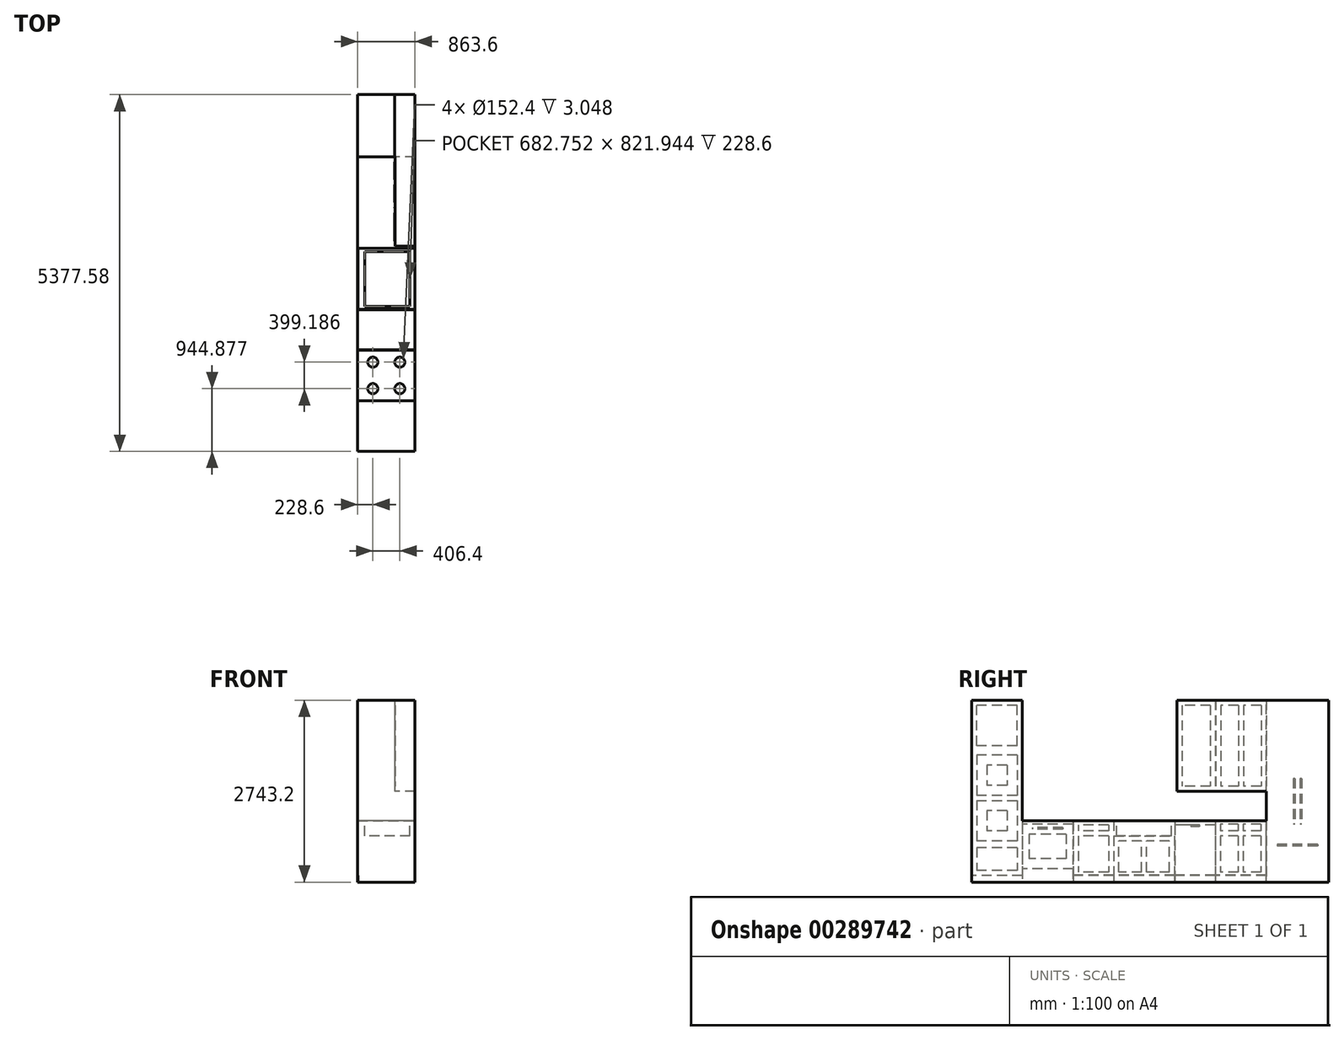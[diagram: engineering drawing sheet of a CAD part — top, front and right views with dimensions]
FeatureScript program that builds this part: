
annotation { "Feature Type Name" : "Feature", "Feature Type Description" : "" }
export const myFeature = defineFeature(function(context is Context, id is Id, definition is map)
    precondition{}
    {
        {
            var Q0;
            Q0=qCreatedBy(makeId("Top.planeOp"),FACE);
            var sketch = newSketch(context, id + "F0", { "sketchPlane" : qUnion([Q0])});
            skLineSegment(sketch, "E0.bottom", {"start": v(431.8, -2688.8) * mm, "end": v(-431.8, -2688.8) * mm});
            skLineSegment(sketch, "E0.top", {"start": v(431.8, 2688.8) * mm, "end": v(-431.8, 2688.8) * mm});
            skLineSegment(sketch, "E0.left", {"start": v(431.8, -2688.8) * mm, "end": v(431.8, 2688.8) * mm});
            skLineSegment(sketch, "E0.right", {"start": v(-431.8, -2688.8) * mm, "end": v(-431.8, 2688.8) * mm});
            skPoint(sketch, "E0.middle", {"position": v(0, 0) * mm});
            skLineSegment(sketch, "E1.bottom", {"start": v(431.8, 1774.4) * mm, "end": v(127, 1774.4) * mm});
            skLineSegment(sketch, "E1.top", {"start": v(431.8, 402.8) * mm, "end": v(127, 402.8) * mm});
            skLineSegment(sketch, "E1.left", {"start": v(431.8, 1774.4) * mm, "end": v(431.8, 402.8) * mm});
            skLineSegment(sketch, "E1.right", {"start": v(127, 1774.4) * mm, "end": v(127, 402.8) * mm});
            skLineSegment(sketch, "E2.top", {"start": v(431.8, 2688.8) * mm, "end": v(127, 2688.8) * mm});
            skLineSegment(sketch, "E2.left", {"start": v(431.8, 1774.4) * mm, "end": v(431.8, 2688.8) * mm});
            skLineSegment(sketch, "E2.right", {"start": v(127, 1774.4) * mm, "end": v(127, 2688.8) * mm});
            skSolve(sketch);
        }
        {
            var Q0;
            {var subQ4=sQuery(id+"F0.wireOp",EDGE,"E1.bottom");Q0=makeQuery(id+"F0.imprint","IMPRINT",FACE,{"disambiguationData":[TD([[makeQuery(id+"F0.imprint","IMPRINT",EDGE,{"derivedFrom":subQ4}),-1.0]])]});}
            var Q1;
            {var subQ0=sQuery(id+"F0.wireOp",EDGE,"E1.bottom");Q1=makeQuery(id+"F0.imprint","IMPRINT",FACE,{"disambiguationData":[TD([[makeQuery(id+"F0.imprint","IMPRINT",EDGE,{"derivedFrom":subQ0}),1.0]])]});}
            var Q2;
            {var subQ1=sQuery(id+"F0.wireOp",EDGE,"E0.bottom");Q2=makeQuery(id+"F0.imprint","IMPRINT",FACE,{"disambiguationData":[TD([[makeQuery(id+"F0.imprint","IMPRINT",EDGE,{"derivedFrom":subQ1}),-1.0]])]});}
            extrude(context, id + "F1", {"entities" : qUnion([Q0, Q1, Q2]), "depth" : 2743.2 * mm, "offsetDistance" : 30.48 * mm});
        }
        {
            var Q0;
            Q0=makeQuery(id+"F1.opExtrude","CAP_FACE",FACE,{"disambiguationData":[OSD([sQuery(id+"F0.wireOp",EDGE,"E0.bottom"),sQuery(id+"F0.wireOp",EDGE,"E0.top"),sQuery(id+"F0.wireOp",EDGE,"E0.left"),sQuery(id+"F0.wireOp",EDGE,"E0.right")])],"isStart":false});
            var sketch = newSketch(context, id + "F2", { "sketchPlane" : qUnion([Q0])});
            skLineSegment(sketch, "E3.bottom", {"start": v(431.8, 2688.8) * mm, "end": v(127, 2688.8) * mm});
            skLineSegment(sketch, "E3.top", {"start": v(431.8, 402.8) * mm, "end": v(127, 402.8) * mm});
            skLineSegment(sketch, "E3.left", {"start": v(431.8, 2688.8) * mm, "end": v(431.8, 402.8) * mm});
            skLineSegment(sketch, "E3.right", {"start": v(127, 2688.8) * mm, "end": v(127, 402.8) * mm});
            skLineSegment(sketch, "E4", {"start": v(127, 1749) * mm, "end": v(-431.8, 1749) * mm});
            skLineSegment(sketch, "E5.bottom", {"start": v(431.8, -2688.8) * mm, "end": v(-431.8, -2688.8) * mm});
            skLineSegment(sketch, "E5.top", {"start": v(431.8, -1926.8) * mm, "end": v(-431.8, -1926.8) * mm});
            skLineSegment(sketch, "E5.left", {"start": v(431.8, -2688.8) * mm, "end": v(431.8, -1926.8) * mm});
            skLineSegment(sketch, "E5.right", {"start": v(-431.8, -2688.8) * mm, "end": v(-431.8, -1926.8) * mm});
            skSolve(sketch);
        }
        {
            var Q0;
            {var subQ3=sQuery(id+"F2.wireOp",EDGE,"E3.top");Q0=makeQuery(id+"F2.imprint","IMPRINT",FACE,{"disambiguationData":[TD([[makeQuery(id+"F2.imprint","IMPRINT",EDGE,{"derivedFrom":subQ3}),1.0]])]});}
            extrude(context, id + "F3", {"entities" : qUnion([Q0]), "operationType" : NewBodyOperationType.REMOVE, "oppositeDirection" : true, "depth" : 1371.6 * mm, "offsetDistance" : 30.48 * mm});
        }
        {
            var Q0;
            {var subQ0=sQuery(id+"F0.wireOp",EDGE,"E0.right");var subQ1=sQuery(id+"F0.wireOp",EDGE,"E0.left");var subQ2=sQuery(id+"F0.wireOp",EDGE,"E0.top");Q0=makeQuery(id+"F3.boolean.opBoolean","SPLIT",FACE,{"disambiguationData":[TD([makeQuery(id+"F1.opExtrude","SWEPT_FACE",FACE,{"disambiguationData":[OSD([subQ2])]})])],"derivedFrom":makeQuery(id+"F1.opExtrude","CAP_FACE",FACE,{"disambiguationData":[OSD([sQuery(id+"F0.wireOp",EDGE,"E0.bottom"),subQ2,subQ1,subQ0])],"isStart":false})});}
            var sketch = newSketch(context, id + "F4", { "sketchPlane" : qUnion([Q0])});
            skLineSegment(sketch, "E6", {"start": v(127, 1749) * mm, "end": v(127, 2688.8) * mm});
            skSolve(sketch);
        }
        {
            var Q0;
            {var subQ0=sQuery(id+"F4.wireOp",EDGE,"E6");Q0=makeQuery(id+"F4.imprint","IMPRINT",FACE,{"disambiguationData":[TD([[makeQuery(id+"F4.imprint","IMPRINT",EDGE,{"derivedFrom":subQ0}),1.0]])]});}
            extrude(context, id + "F5", {"entities" : qUnion([Q0]), "operationType" : NewBodyOperationType.REMOVE, "oppositeDirection" : true, "depth" : (((9 * 12) - 70.5) / 12) * mm, "offsetDistance" : 30.48 * mm});
        }
        {
            var Q0;
            Q0=makeQuery(id+"F1.opExtrude","SWEPT_FACE",FACE,{"disambiguationData":[OSD([sQuery(id+"F0.wireOp",EDGE,"E0.right")])]});
            var sketch = newSketch(context, id + "F6", { "sketchPlane" : qUnion([Q0])});
            skLineSegment(sketch, "E7", {"start": v(-1749, 1371.6) * mm, "end": v(-1749, 927.1) * mm});
            skLineSegment(sketch, "E8", {"start": v(-1749, 927.1) * mm, "end": v(1926.8, 927.1) * mm});
            skLineSegment(sketch, "E9", {"start": v(1926.8, 927.1) * mm, "end": v(1926.8, 1371.6) * mm});
            skSolve(sketch);
        }
        {
            var Q0;
            Q0=makeQuery(id+"F6.imprint","IMPRINT",FACE,{"disambiguationData":[TD([[makeQuery(id+"F6.imprint","IMPRINT",EDGE,{"derivedFrom":sQuery(id+"F6.wireOp",EDGE,"E7")}),1.0]])]});
            extrude(context, id + "F7", {"entities" : qUnion([Q0]), "operationType" : NewBodyOperationType.REMOVE, "oppositeDirection" : true, "depth" : 1219.2 * mm, "offsetDistance" : 30.48 * mm});
        }
        {
            var Q0;
            Q0=makeQuery(id+"F1.opExtrude","SWEPT_FACE",FACE,{"disambiguationData":[OSD([sQuery(id+"F0.wireOp",EDGE,"E0.right")])]});
            var sketch = newSketch(context, id + "F8", { "sketchPlane" : qUnion([Q0])});
            skLineSegment(sketch, "E10.bottom", {"start": v(-2282.4, 1562.1) * mm, "end": v(-2257, 1562.1) * mm});
            skLineSegment(sketch, "E10.top", {"start": v(-2282.4, 876.3) * mm, "end": v(-2257, 876.3) * mm});
            skLineSegment(sketch, "E10.left", {"start": v(-2282.4, 1562.1) * mm, "end": v(-2282.4, 876.3) * mm});
            skLineSegment(sketch, "E10.right", {"start": v(-2257, 1562.1) * mm, "end": v(-2257, 876.3) * mm});
            skLineSegment(sketch, "E11.bottom", {"start": v(-2180.8, 1562.1) * mm, "end": v(-2155.4, 1562.1) * mm});
            skLineSegment(sketch, "E11.top", {"start": v(-2180.8, 876.3) * mm, "end": v(-2155.4, 876.3) * mm});
            skLineSegment(sketch, "E11.left", {"start": v(-2180.8, 1562.1) * mm, "end": v(-2180.8, 876.3) * mm});
            skLineSegment(sketch, "E11.right", {"start": v(-2155.4, 1562.1) * mm, "end": v(-2155.4, 876.3) * mm});
            skLineSegment(sketch, "E12", {"start": v(-2218.9, 1790.7) * mm, "end": v(-2218.9, 0) * mm, "construction": true});
            skLineSegment(sketch, "E13.bottom", {"start": v(-2523.7, 571.5) * mm, "end": v(-1914.1, 571.5) * mm});
            skLineSegment(sketch, "E13.top", {"start": v(-2523.7, 546.1) * mm, "end": v(-1914.1, 546.1) * mm});
            skLineSegment(sketch, "E13.left", {"start": v(-2523.7, 571.5) * mm, "end": v(-2523.7, 546.1) * mm});
            skLineSegment(sketch, "E13.right", {"start": v(-1914.1, 571.5) * mm, "end": v(-1914.1, 546.1) * mm});
            skLineSegment(sketch, "E14.left", {"start": v(-1749, 927.1) * mm, "end": v(-1749, 0) * mm});
            skLineSegment(sketch, "E14.right", {"start": v(-1745.95, 927.1) * mm, "end": v(-1745.95, 0) * mm});
            skLineSegment(sketch, "E15.left", {"start": v(-983.95, 927.1) * mm, "end": v(-983.95, 0) * mm});
            skLineSegment(sketch, "E15.right", {"start": v(-980.9, 927.1) * mm, "end": v(-980.9, 0) * mm});
            skLineSegment(sketch, "E16.bottom", {"start": v(-371.3, 927.1) * mm, "end": v(-368.25, 927.1) * mm});
            skLineSegment(sketch, "E16.top", {"start": v(-371.3, 0) * mm, "end": v(-368.25, 0) * mm});
            skLineSegment(sketch, "E16.left", {"start": v(-371.3, 927.1) * mm, "end": v(-371.3, 0) * mm});
            skLineSegment(sketch, "E16.right", {"start": v(-368.25, 927.1) * mm, "end": v(-368.25, 0) * mm});
            skLineSegment(sketch, "E17.bottom", {"start": v(546.15, 927.1) * mm, "end": v(549.2, 927.1) * mm});
            skLineSegment(sketch, "E17.top", {"start": v(546.15, 0) * mm, "end": v(549.2, 0) * mm});
            skLineSegment(sketch, "E17.left", {"start": v(546.15, 927.1) * mm, "end": v(546.15, 0) * mm});
            skLineSegment(sketch, "E17.right", {"start": v(549.2, 927.1) * mm, "end": v(549.2, 0) * mm});
            skLineSegment(sketch, "E18.bottom", {"start": v(1158.8, 927.1) * mm, "end": v(1161.85, 927.1) * mm});
            skLineSegment(sketch, "E18.top", {"start": v(1158.8, 0) * mm, "end": v(1161.85, 0) * mm});
            skLineSegment(sketch, "E18.left", {"start": v(1158.8, 927.1) * mm, "end": v(1158.8, 0) * mm});
            skLineSegment(sketch, "E18.right", {"start": v(1161.85, 927.1) * mm, "end": v(1161.85, 0) * mm});
            skLineSegment(sketch, "E19.bottom", {"start": v(1923.85, 927.1) * mm, "end": v(1926.9, 927.1) * mm});
            skLineSegment(sketch, "E19.top", {"start": v(1923.85, 0) * mm, "end": v(1926.9, 0) * mm});
            skLineSegment(sketch, "E19.left", {"start": v(1923.85, 927.1) * mm, "end": v(1923.85, 0) * mm});
            skLineSegment(sketch, "E19.right", {"start": v(1926.9, 927.1) * mm, "end": v(1926.9, 0) * mm});
            skLineSegment(sketch, "E20.bottom", {"start": v(-1669.75, 876.3) * mm, "end": v(-1403.05, 876.3) * mm});
            skLineSegment(sketch, "E20.top", {"start": v(-1669.75, 774.7) * mm, "end": v(-1403.05, 774.7) * mm});
            skLineSegment(sketch, "E20.left", {"start": v(-1669.75, 876.3) * mm, "end": v(-1669.75, 774.7) * mm});
            skLineSegment(sketch, "E20.right", {"start": v(-1403.05, 876.3) * mm, "end": v(-1403.05, 774.7) * mm});
            skLineSegment(sketch, "E21.bottom", {"start": v(-1326.85, 876.3) * mm, "end": v(-1060.15, 876.3) * mm});
            skLineSegment(sketch, "E21.top", {"start": v(-1326.85, 774.7) * mm, "end": v(-1060.15, 774.7) * mm});
            skLineSegment(sketch, "E21.left", {"start": v(-1326.85, 876.3) * mm, "end": v(-1326.85, 774.7) * mm});
            skLineSegment(sketch, "E21.right", {"start": v(-1060.15, 876.3) * mm, "end": v(-1060.15, 774.7) * mm});
            skLineSegment(sketch, "E22", {"start": v(-1364.95, 927.1) * mm, "end": v(-1364.95, 0) * mm, "construction": true});
            skLineSegment(sketch, "E23.bottom", {"start": v(-1669.75, 698.5) * mm, "end": v(-1403.05, 698.5) * mm});
            skLineSegment(sketch, "E23.top", {"start": v(-1669.75, 152.4) * mm, "end": v(-1403.05, 152.4) * mm});
            skLineSegment(sketch, "E23.left", {"start": v(-1669.75, 698.5) * mm, "end": v(-1669.75, 152.4) * mm});
            skLineSegment(sketch, "E23.right", {"start": v(-1403.05, 698.5) * mm, "end": v(-1403.05, 152.4) * mm});
            skLineSegment(sketch, "E24.bottom", {"start": v(-1326.85, 698.5) * mm, "end": v(-1060.15, 698.5) * mm});
            skLineSegment(sketch, "E24.top", {"start": v(-1326.85, 152.4) * mm, "end": v(-1060.15, 152.4) * mm});
            skLineSegment(sketch, "E24.left", {"start": v(-1326.85, 698.5) * mm, "end": v(-1326.85, 152.4) * mm});
            skLineSegment(sketch, "E24.right", {"start": v(-1060.15, 698.5) * mm, "end": v(-1060.15, 152.4) * mm});
            skLineSegment(sketch, "E25.bottom", {"start": v(-980.9, 863.6) * mm, "end": v(-371.3, 863.6) * mm});
            skLineSegment(sketch, "E25.top", {"start": v(-980.9, 860.55) * mm, "end": v(-371.3, 860.55) * mm});
            skLineSegment(sketch, "E25.left", {"start": v(-980.9, 863.6) * mm, "end": v(-980.9, 860.55) * mm});
            skLineSegment(sketch, "E25.right", {"start": v(-371.3, 863.6) * mm, "end": v(-371.3, 860.55) * mm});
            skLineSegment(sketch, "E26.bottom", {"start": v(-739.6, 860.55) * mm, "end": v(-612.6, 860.55) * mm});
            skLineSegment(sketch, "E26.top", {"start": v(-739.6, 835.15) * mm, "end": v(-612.6, 835.15) * mm});
            skLineSegment(sketch, "E26.left", {"start": v(-739.6, 860.55) * mm, "end": v(-739.6, 835.15) * mm});
            skLineSegment(sketch, "E26.right", {"start": v(-612.6, 860.55) * mm, "end": v(-612.6, 835.15) * mm});
            skLineSegment(sketch, "E27", {"start": v(-676.1, 927.1) * mm, "end": v(-676.1, 0) * mm, "construction": true});
            skLineSegment(sketch, "E28.bottom", {"start": v(-980.9, 104.65) * mm, "end": v(-371.3, 104.65) * mm});
            skLineSegment(sketch, "E28.top", {"start": v(-980.9, 101.6) * mm, "end": v(-371.3, 101.6) * mm});
            skLineSegment(sketch, "E28.left", {"start": v(-980.9, 104.65) * mm, "end": v(-980.9, 101.6) * mm});
            skLineSegment(sketch, "E28.right", {"start": v(-371.3, 104.65) * mm, "end": v(-371.3, 101.6) * mm});
            skLineSegment(sketch, "E29.bottom", {"start": v(546.15, 698.5) * mm, "end": v(-368.25, 698.5) * mm});
            skLineSegment(sketch, "E29.top", {"start": v(546.15, 695.45) * mm, "end": v(-368.25, 695.45) * mm});
            skLineSegment(sketch, "E29.left", {"start": v(546.15, 698.5) * mm, "end": v(546.15, 695.45) * mm});
            skLineSegment(sketch, "E29.right", {"start": v(-368.25, 698.5) * mm, "end": v(-368.25, 695.45) * mm});
            skLineSegment(sketch, "E30.bottom", {"start": v(-292.05, 152.4) * mm, "end": v(50.85, 152.4) * mm});
            skLineSegment(sketch, "E30.top", {"start": v(-292.05, 619.25) * mm, "end": v(50.85, 619.25) * mm});
            skLineSegment(sketch, "E30.left", {"start": v(-292.05, 152.4) * mm, "end": v(-292.05, 619.25) * mm});
            skLineSegment(sketch, "E30.right", {"start": v(50.85, 152.4) * mm, "end": v(50.85, 619.25) * mm});
            skLineSegment(sketch, "E31.bottom", {"start": v(127.05, 152.4) * mm, "end": v(469.95, 152.4) * mm});
            skLineSegment(sketch, "E31.top", {"start": v(127.05, 619.25) * mm, "end": v(469.95, 619.25) * mm});
            skLineSegment(sketch, "E31.left", {"start": v(127.05, 152.4) * mm, "end": v(127.05, 619.25) * mm});
            skLineSegment(sketch, "E31.right", {"start": v(469.95, 152.4) * mm, "end": v(469.95, 619.25) * mm});
            skLineSegment(sketch, "E32", {"start": v(88.95, 695.45) * mm, "end": v(88.95, 0) * mm, "construction": true});
            skLineSegment(sketch, "E33.bottom", {"start": v(-1745.95, 104.65) * mm, "end": v(-983.95, 104.65) * mm});
            skLineSegment(sketch, "E33.top", {"start": v(-1745.95, 101.6) * mm, "end": v(-983.95, 101.6) * mm});
            skLineSegment(sketch, "E33.left", {"start": v(-1745.95, 104.65) * mm, "end": v(-1745.95, 101.6) * mm});
            skLineSegment(sketch, "E33.right", {"start": v(-983.95, 104.65) * mm, "end": v(-983.95, 101.6) * mm});
            skLineSegment(sketch, "E34.bottom", {"start": v(-368.25, 104.65) * mm, "end": v(546.15, 104.65) * mm});
            skLineSegment(sketch, "E34.top", {"start": v(-368.25, 101.6) * mm, "end": v(546.15, 101.6) * mm});
            skLineSegment(sketch, "E34.left", {"start": v(-368.25, 104.65) * mm, "end": v(-368.25, 101.6) * mm});
            skLineSegment(sketch, "E34.right", {"start": v(546.15, 104.65) * mm, "end": v(546.15, 101.6) * mm});
            skLineSegment(sketch, "E35.bottom", {"start": v(625.4, 860.55) * mm, "end": v(1082.6, 860.55) * mm});
            skLineSegment(sketch, "E35.top", {"start": v(625.4, 774.7) * mm, "end": v(1082.6, 774.7) * mm});
            skLineSegment(sketch, "E35.left", {"start": v(625.4, 860.55) * mm, "end": v(625.4, 774.7) * mm});
            skLineSegment(sketch, "E35.right", {"start": v(1082.6, 860.55) * mm, "end": v(1082.6, 774.7) * mm});
            skLineSegment(sketch, "E36.bottom", {"start": v(625.4, 698.5) * mm, "end": v(1082.6, 698.5) * mm});
            skLineSegment(sketch, "E36.top", {"start": v(625.4, 152.4) * mm, "end": v(1082.6, 152.4) * mm});
            skLineSegment(sketch, "E36.left", {"start": v(625.4, 698.5) * mm, "end": v(625.4, 152.4) * mm});
            skLineSegment(sketch, "E36.right", {"start": v(1082.6, 698.5) * mm, "end": v(1082.6, 152.4) * mm});
            skLineSegment(sketch, "E37.bottom", {"start": v(549.2, 104.65) * mm, "end": v(1158.8, 104.65) * mm});
            skLineSegment(sketch, "E37.top", {"start": v(549.2, 101.6) * mm, "end": v(1158.8, 101.6) * mm});
            skLineSegment(sketch, "E37.left", {"start": v(549.2, 104.65) * mm, "end": v(549.2, 101.6) * mm});
            skLineSegment(sketch, "E37.right", {"start": v(1158.8, 104.65) * mm, "end": v(1158.8, 101.6) * mm});
            skLineSegment(sketch, "E38.bottom", {"start": v(1161.85, 876.3) * mm, "end": v(1923.85, 876.3) * mm});
            skLineSegment(sketch, "E38.top", {"start": v(1161.85, 873.25) * mm, "end": v(1923.85, 873.25) * mm});
            skLineSegment(sketch, "E38.left", {"start": v(1161.85, 876.3) * mm, "end": v(1161.85, 873.25) * mm});
            skLineSegment(sketch, "E38.right", {"start": v(1923.85, 876.3) * mm, "end": v(1923.85, 873.25) * mm});
            skLineSegment(sketch, "E39.bottom", {"start": v(1314.25, 825.5) * mm, "end": v(1771.45, 825.5) * mm});
            skLineSegment(sketch, "E39.top", {"start": v(1314.25, 800.1) * mm, "end": v(1771.45, 800.1) * mm});
            skLineSegment(sketch, "E39.left", {"start": v(1314.25, 825.5) * mm, "end": v(1314.25, 800.1) * mm});
            skLineSegment(sketch, "E39.right", {"start": v(1771.45, 825.5) * mm, "end": v(1771.45, 800.1) * mm});
            skLineSegment(sketch, "E40", {"start": v(1542.85, 825.5) * mm, "end": v(1542.85, 353.37) * mm, "construction": true});
            skLineSegment(sketch, "E41.bottom", {"start": v(1161.85, 203.2) * mm, "end": v(1923.85, 203.2) * mm});
            skLineSegment(sketch, "E41.top", {"start": v(1161.85, 200.15) * mm, "end": v(1923.85, 200.15) * mm});
            skLineSegment(sketch, "E41.left", {"start": v(1161.85, 203.2) * mm, "end": v(1161.85, 200.15) * mm});
            skLineSegment(sketch, "E41.right", {"start": v(1923.85, 203.2) * mm, "end": v(1923.85, 200.15) * mm});
            skLineSegment(sketch, "E42.bottom", {"start": v(1263.45, 723.9) * mm, "end": v(1822.25, 723.9) * mm});
            skLineSegment(sketch, "E42.top", {"start": v(1263.45, 355.6) * mm, "end": v(1822.25, 355.6) * mm});
            skLineSegment(sketch, "E42.left", {"start": v(1263.45, 723.9) * mm, "end": v(1263.45, 355.6) * mm});
            skLineSegment(sketch, "E42.right", {"start": v(1822.25, 723.9) * mm, "end": v(1822.25, 355.6) * mm});
            skSolve(sketch);
        }
        {
            var Q0;
            Q0=makeQuery(id+"F8.imprint","IMPRINT",FACE,{"disambiguationData":[TD([[makeQuery(id+"F8.imprint","IMPRINT",EDGE,{"derivedFrom":sQuery(id+"F8.wireOp",EDGE,"E10.bottom")}),-1.0]])]});
            var Q1;
            Q1=makeQuery(id+"F8.imprint","IMPRINT",FACE,{"disambiguationData":[TD([[makeQuery(id+"F8.imprint","IMPRINT",EDGE,{"derivedFrom":sQuery(id+"F8.wireOp",EDGE,"E11.bottom")}),-1.0]])]});
            var Q2;
            Q2=makeQuery(id+"F8.imprint","IMPRINT",FACE,{"disambiguationData":[TD([[makeQuery(id+"F8.imprint","IMPRINT",EDGE,{"derivedFrom":sQuery(id+"F8.wireOp",EDGE,"E13.bottom")}),-1.0]])]});
            var Q3;
            Q3=makeQuery(id+"F8.imprint","IMPRINT",FACE,{"disambiguationData":[TD([[makeQuery(id+"F8.imprint","IMPRINT",EDGE,{"derivedFrom":sQuery(id+"F8.wireOp",EDGE,"E14.bottom")}),-1.0]])]});
            var Q4;
            Q4=makeQuery(id+"F8.imprint","IMPRINT",FACE,{"disambiguationData":[TD([[makeQuery(id+"F8.imprint","IMPRINT",EDGE,{"derivedFrom":sQuery(id+"F8.wireOp",EDGE,"E15.bottom")}),-1.0]])]});
            var Q5;
            Q5=makeQuery(id+"F8.imprint","IMPRINT",FACE,{"disambiguationData":[TD([[makeQuery(id+"F8.imprint","IMPRINT",EDGE,{"derivedFrom":sQuery(id+"F8.wireOp",EDGE,"E16.bottom")}),-1.0]])]});
            var Q6;
            Q6=makeQuery(id+"F8.imprint","IMPRINT",FACE,{"disambiguationData":[TD([[makeQuery(id+"F8.imprint","IMPRINT",EDGE,{"derivedFrom":sQuery(id+"F8.wireOp",EDGE,"E17.bottom")}),-1.0]])]});
            var Q7;
            Q7=makeQuery(id+"F8.imprint","IMPRINT",FACE,{"disambiguationData":[TD([[makeQuery(id+"F8.imprint","IMPRINT",EDGE,{"derivedFrom":sQuery(id+"F8.wireOp",EDGE,"E18.bottom")}),-1.0]])]});
            var Q8;
            Q8=makeQuery(id+"F8.imprint","IMPRINT",FACE,{"disambiguationData":[TD([[makeQuery(id+"F8.imprint","IMPRINT",EDGE,{"derivedFrom":sQuery(id+"F8.wireOp",EDGE,"E19.bottom")}),-1.0]])]});
            var Q9;
            {var subQ0=sQuery(id+"F8.wireOp",EDGE,"JCAVA3rn-6h3x-s8vH-r6hd-8YxRRoSe079N.bottom");Q9=makeQuery(id+"F8.imprint","IMPRINT",FACE,{"disambiguationData":[TD([[makeQuery(id+"F8.imprint","IMPRINT",EDGE,{"derivedFrom":subQ0}),1.0]])]});}
            var Q10;
            Q10=makeQuery(id+"F8.imprint","IMPRINT",FACE,{"disambiguationData":[TD([[makeQuery(id+"F8.imprint","IMPRINT",EDGE,{"derivedFrom":sQuery(id+"F8.wireOp",EDGE,"2RqrLUwl-DQjW-4bsu-7qjS-rTvcbJywuATo.bottom")}),-1.0]])]});
            var Q11;
            Q11=makeQuery(id+"F8.imprint","IMPRINT",FACE,{"disambiguationData":[TD([[makeQuery(id+"F8.imprint","IMPRINT",EDGE,{"derivedFrom":sQuery(id+"F8.wireOp",EDGE,"SJMlzqgD-H88F-8DKG-ENUh-f2WFZTCTSlYQ.bottom")}),-1.0]])]});
            var Q12;
            {var subQ0=sQuery(id+"F8.wireOp",EDGE,"qLF5KBOE-7xnm-FECH-9X16-jm7sObQ1of7a.bottom");Q12=makeQuery(id+"F8.imprint","IMPRINT",FACE,{"disambiguationData":[TD([[makeQuery(id+"F8.imprint","IMPRINT",EDGE,{"derivedFrom":subQ0}),-1.0]])]});}
            var Q13;
            {var subQ0=sQuery(id+"F8.wireOp",EDGE,"E14.left");Q13=makeQuery(id+"F8.imprint","IMPRINT",FACE,{"disambiguationData":[TD([[makeQuery(id+"F8.imprint","IMPRINT",EDGE,{"derivedFrom":subQ0}),1.0]])]});}
            var Q14;
            Q14=makeQuery(id+"F8.imprint","IMPRINT",FACE,{"disambiguationData":[TD([[makeQuery(id+"F8.imprint","IMPRINT",EDGE,{"derivedFrom":sQuery(id+"F8.wireOp",EDGE,"E20.bottom")}),-1.0]])]});
            var Q15;
            Q15=makeQuery(id+"F8.imprint","IMPRINT",FACE,{"disambiguationData":[TD([[makeQuery(id+"F8.imprint","IMPRINT",EDGE,{"derivedFrom":sQuery(id+"F8.wireOp",EDGE,"E21.bottom")}),-1.0]])]});
            var Q16;
            Q16=makeQuery(id+"F8.imprint","IMPRINT",FACE,{"disambiguationData":[TD([[makeQuery(id+"F8.imprint","IMPRINT",EDGE,{"derivedFrom":sQuery(id+"F8.wireOp",EDGE,"E23.bottom")}),-1.0]])]});
            var Q17;
            Q17=makeQuery(id+"F8.imprint","IMPRINT",FACE,{"disambiguationData":[TD([[makeQuery(id+"F8.imprint","IMPRINT",EDGE,{"derivedFrom":sQuery(id+"F8.wireOp",EDGE,"E24.bottom")}),-1.0]])]});
            var Q18;
            {var subQ9=sQuery(id+"F8.wireOp",EDGE,"E15.left");Q18=makeQuery(id+"F8.imprint","IMPRINT",FACE,{"disambiguationData":[TD([[makeQuery(id+"F8.imprint","IMPRINT",EDGE,{"derivedFrom":subQ9}),1.0]])]});}
            var Q19;
            {var subQ0=sQuery(id+"F8.wireOp",EDGE,"E25.bottom");Q19=makeQuery(id+"F8.imprint","IMPRINT",FACE,{"disambiguationData":[TD([[makeQuery(id+"F8.imprint","IMPRINT",EDGE,{"derivedFrom":subQ0}),-1.0]])]});}
            var Q20;
            Q20=makeQuery(id+"F8.imprint","IMPRINT",FACE,{"disambiguationData":[TD([[makeQuery(id+"F8.imprint","IMPRINT",EDGE,{"derivedFrom":sQuery(id+"F8.wireOp",EDGE,"E26.top")}),1.0]])]});
            var Q21;
            {var subQ2=sQuery(id+"F8.wireOp",EDGE,"E28.bottom");Q21=makeQuery(id+"F8.imprint","IMPRINT",FACE,{"disambiguationData":[TD([[makeQuery(id+"F8.imprint","IMPRINT",EDGE,{"derivedFrom":subQ2}),-1.0]])]});}
            var Q22;
            Q22=makeQuery(id+"F8.imprint","IMPRINT",FACE,{"disambiguationData":[TD([[makeQuery(id+"F8.imprint","IMPRINT",EDGE,{"derivedFrom":sQuery(id+"F8.wireOp",EDGE,"E30.bottom")}),1.0]])]});
            var Q23;
            Q23=makeQuery(id+"F8.imprint","IMPRINT",FACE,{"disambiguationData":[TD([[makeQuery(id+"F8.imprint","IMPRINT",EDGE,{"derivedFrom":sQuery(id+"F8.wireOp",EDGE,"E31.bottom")}),1.0]])]});
            var Q24;
            {var subQ3=sQuery(id+"F8.wireOp",EDGE,"E29.bottom");Q24=makeQuery(id+"F8.imprint","IMPRINT",FACE,{"disambiguationData":[TD([[makeQuery(id+"F8.imprint","IMPRINT",EDGE,{"derivedFrom":subQ3}),-1.0]])]});}
            var Q25;
            {var subQ2=sQuery(id+"F8.wireOp",EDGE,"E33.bottom");Q25=makeQuery(id+"F8.imprint","IMPRINT",FACE,{"disambiguationData":[TD([[makeQuery(id+"F8.imprint","IMPRINT",EDGE,{"derivedFrom":subQ2}),-1.0]])]});}
            var Q26;
            {var subQ0=sQuery(id+"F8.wireOp",EDGE,"E34.bottom");Q26=makeQuery(id+"F8.imprint","IMPRINT",FACE,{"disambiguationData":[TD([[makeQuery(id+"F8.imprint","IMPRINT",EDGE,{"derivedFrom":subQ0}),-1.0]])]});}
            var Q27;
            Q27=makeQuery(id+"F8.imprint","IMPRINT",FACE,{"disambiguationData":[TD([[makeQuery(id+"F8.imprint","IMPRINT",EDGE,{"derivedFrom":sQuery(id+"F8.wireOp",EDGE,"E35.bottom")}),-1.0]])]});
            var Q28;
            Q28=makeQuery(id+"F8.imprint","IMPRINT",FACE,{"disambiguationData":[TD([[makeQuery(id+"F8.imprint","IMPRINT",EDGE,{"derivedFrom":sQuery(id+"F8.wireOp",EDGE,"E36.bottom")}),-1.0]])]});
            var Q29;
            {var subQ2=sQuery(id+"F8.wireOp",EDGE,"E37.bottom");Q29=makeQuery(id+"F8.imprint","IMPRINT",FACE,{"disambiguationData":[TD([[makeQuery(id+"F8.imprint","IMPRINT",EDGE,{"derivedFrom":subQ2}),-1.0]])]});}
            var Q30;
            {var subQ0=sQuery(id+"F8.wireOp",EDGE,"E41.bottom");Q30=makeQuery(id+"F8.imprint","IMPRINT",FACE,{"disambiguationData":[TD([[makeQuery(id+"F8.imprint","IMPRINT",EDGE,{"derivedFrom":subQ0}),-1.0]])]});}
            var Q31;
            Q31=makeQuery(id+"F8.imprint","IMPRINT",FACE,{"disambiguationData":[TD([[makeQuery(id+"F8.imprint","IMPRINT",EDGE,{"derivedFrom":sQuery(id+"F8.wireOp",EDGE,"E42.bottom")}),-1.0]])]});
            var Q32;
            Q32=makeQuery(id+"F8.imprint","IMPRINT",FACE,{"disambiguationData":[TD([[makeQuery(id+"F8.imprint","IMPRINT",EDGE,{"derivedFrom":sQuery(id+"F8.wireOp",EDGE,"E39.bottom")}),-1.0]])]});
            var Q33;
            {var subQ2=sQuery(id+"F8.wireOp",EDGE,"E38.bottom");Q33=makeQuery(id+"F8.imprint","IMPRINT",FACE,{"disambiguationData":[TD([[makeQuery(id+"F8.imprint","IMPRINT",EDGE,{"derivedFrom":subQ2}),-1.0]])]});}
            extrude(context, id + "F9", {"entities" : qUnion([Q0, Q1, Q2, Q3, Q4, Q5, Q6, Q7, Q8, Q9, Q10, Q11, Q12, Q13, Q14, Q15, Q16, Q17, Q18, Q19, Q20, Q21, Q22, Q23, Q24, Q25, Q26, Q27, Q28, Q29, Q30, Q31, Q32, Q33]), "operationType" : NewBodyOperationType.REMOVE, "oppositeDirection" : true, "depth" : 3.05 * mm, "offsetDistance" : 30.48 * mm});
        }
        {
            var Q0;
            Q0=makeQuery(id+"F5.boolean.opBoolean","MERGE",FACE,{"derivedFrom":[makeQuery(id+"F3.boolean.opBoolean","COPY",FACE,{"derivedFrom":makeQuery(id+"F3.opExtrude","SWEPT_FACE",FACE,{"disambiguationData":[OSD([sQuery(id+"F2.wireOp",EDGE,"E3.right")])]})})],"fromTools":[makeQuery(id+"F5.opExtrude","SWEPT_FACE",FACE,{"disambiguationData":[OSD([sQuery(id+"F4.wireOp",EDGE,"E6")])]})]});
            var sketch = newSketch(context, id + "F10", { "sketchPlane" : qUnion([Q0])});
            skLineSegment(sketch, "E43.bottom", {"start": v(-2612.6, 2667) * mm, "end": v(-2257, 2667) * mm});
            skLineSegment(sketch, "E43.top", {"start": v(-2612.6, 1866.9) * mm, "end": v(-2257, 1866.9) * mm});
            skLineSegment(sketch, "E43.left", {"start": v(-2612.6, 2667) * mm, "end": v(-2612.6, 1866.9) * mm});
            skLineSegment(sketch, "E43.right", {"start": v(-2257, 2667) * mm, "end": v(-2257, 1866.9) * mm});
            skLineSegment(sketch, "E44.bottom", {"start": v(-2180.8, 2667) * mm, "end": v(-1825.2, 2667) * mm});
            skLineSegment(sketch, "E44.top", {"start": v(-2180.8, 1866.9) * mm, "end": v(-1825.2, 1866.9) * mm});
            skLineSegment(sketch, "E44.left", {"start": v(-2180.8, 2667) * mm, "end": v(-2180.8, 1866.9) * mm});
            skLineSegment(sketch, "E44.right", {"start": v(-1825.2, 2667) * mm, "end": v(-1825.2, 1866.9) * mm});
            skLineSegment(sketch, "E45", {"start": v(-2218.9, 1790.7) * mm, "end": v(-2218.9, 2743.2) * mm, "construction": true});
            skLineSegment(sketch, "E46.bottom", {"start": v(-1672.8, 2667) * mm, "end": v(-1406.1, 2667) * mm});
            skLineSegment(sketch, "E46.top", {"start": v(-1672.8, 1447.8) * mm, "end": v(-1406.1, 1447.8) * mm});
            skLineSegment(sketch, "E46.left", {"start": v(-1672.8, 2667) * mm, "end": v(-1672.8, 1447.8) * mm});
            skLineSegment(sketch, "E46.right", {"start": v(-1406.1, 2667) * mm, "end": v(-1406.1, 1447.8) * mm});
            skLineSegment(sketch, "E47.bottom", {"start": v(-1329.9, 2667) * mm, "end": v(-1063.2, 2667) * mm});
            skLineSegment(sketch, "E47.top", {"start": v(-1329.9, 1447.8) * mm, "end": v(-1063.2, 1447.8) * mm});
            skLineSegment(sketch, "E47.left", {"start": v(-1329.9, 2667) * mm, "end": v(-1329.9, 1447.8) * mm});
            skLineSegment(sketch, "E47.right", {"start": v(-1063.2, 2667) * mm, "end": v(-1063.2, 1447.8) * mm});
            skLineSegment(sketch, "E48.bottom", {"start": v(-907.75, 2667) * mm, "end": v(-479, 2667) * mm});
            skLineSegment(sketch, "E48.top", {"start": v(-907.75, 1447.8) * mm, "end": v(-479, 1447.8) * mm});
            skLineSegment(sketch, "E48.left", {"start": v(-907.75, 2667) * mm, "end": v(-907.75, 1447.8) * mm});
            skLineSegment(sketch, "E48.right", {"start": v(-479, 2667) * mm, "end": v(-479, 1447.8) * mm});
            skLineSegment(sketch, "E49", {"start": v(-1749, 1371.6) * mm, "end": v(-1368, 1371.6) * mm, "construction": true});
            skLineSegment(sketch, "E50.bottom", {"start": v(-1752.04, 2743.2) * mm, "end": v(-1749, 2743.2) * mm});
            skLineSegment(sketch, "E50.top", {"start": v(-1752.04, 1790.7) * mm, "end": v(-1749, 1790.7) * mm});
            skLineSegment(sketch, "E50.left", {"start": v(-1752.04, 2743.2) * mm, "end": v(-1752.04, 1790.7) * mm});
            skLineSegment(sketch, "E50.right", {"start": v(-1749, 2743.2) * mm, "end": v(-1749, 1790.7) * mm});
            skLineSegment(sketch, "E51.bottom", {"start": v(-987, 2743.2) * mm, "end": v(-983.95, 2743.2) * mm});
            skLineSegment(sketch, "E51.top", {"start": v(-987, 1371.6) * mm, "end": v(-983.95, 1371.6) * mm});
            skLineSegment(sketch, "E51.left", {"start": v(-987, 2743.2) * mm, "end": v(-987, 1371.6) * mm});
            skLineSegment(sketch, "E51.right", {"start": v(-983.95, 2743.2) * mm, "end": v(-983.95, 1371.6) * mm});
            skSolve(sketch);
        }
        {
            var Q0;
            Q0=makeQuery(id+"F10.imprint","IMPRINT",FACE,{"disambiguationData":[TD([[makeQuery(id+"F10.imprint","IMPRINT",EDGE,{"derivedFrom":sQuery(id+"F10.wireOp",EDGE,"E43.bottom")}),1.0]])]});
            var Q1;
            Q1=makeQuery(id+"F10.imprint","IMPRINT",FACE,{"disambiguationData":[TD([[makeQuery(id+"F10.imprint","IMPRINT",EDGE,{"derivedFrom":sQuery(id+"F10.wireOp",EDGE,"E46.bottom")}),1.0]])]});
            var Q2;
            Q2=makeQuery(id+"F10.imprint","IMPRINT",FACE,{"disambiguationData":[TD([[makeQuery(id+"F10.imprint","IMPRINT",EDGE,{"derivedFrom":sQuery(id+"F10.wireOp",EDGE,"E48.bottom")}),1.0]])]});
            extrude(context, id + "F11", {"entities" : qUnion([Q0, Q1, Q2]), "operationType" : NewBodyOperationType.REMOVE, "oppositeDirection" : true, "depth" : 3.05 * mm, "offsetDistance" : 30.48 * mm});
        }
        {
            var Q0;
            Q0=makeQuery(id+"F7.boolean.opBoolean","COPY",FACE,{"derivedFrom":makeQuery(id+"F7.opExtrude","SWEPT_FACE",FACE,{"disambiguationData":[OSD([sQuery(id+"F6.wireOp",EDGE,"E8")])]})});
            var sketch = newSketch(context, id + "F12", { "sketchPlane" : qUnion([Q0])});
            skLineSegment(sketch, "E52", {"start": v(-428.75, 371.3) * mm, "end": v(431.8, 371.3) * mm});
            skLineSegment(sketch, "E53", {"start": v(431.8, 374.35) * mm, "end": v(-431.8, 374.35) * mm});
            skLineSegment(sketch, "E54", {"start": v(-428.75, -549.2) * mm, "end": v(431.8, -549.2) * mm});
            skLineSegment(sketch, "E55", {"start": v(431.8, -552.25) * mm, "end": v(-431.8, -552.25) * mm});
            skLineSegment(sketch, "E56.bottom", {"start": v(-428.75, -1161.85) * mm, "end": v(431.8, -1161.85) * mm});
            skLineSegment(sketch, "E56.top", {"start": v(-428.75, -1158.8) * mm, "end": v(431.8, -1158.8) * mm});
            skLineSegment(sketch, "E56.left", {"start": v(-428.75, -1161.85) * mm, "end": v(-428.75, -1158.8) * mm});
            skLineSegment(sketch, "E56.right", {"start": v(431.8, -1161.85) * mm, "end": v(431.8, -1158.8) * mm});
            skSolve(sketch);
        }
        {
            var Q0;
            {var subQ0=sQuery(id+"F12.wireOp",EDGE,"E52");Q0=makeQuery(id+"F12.imprint","IMPRINT",FACE,{"disambiguationData":[TD([[makeQuery(id+"F12.imprint","IMPRINT",EDGE,{"derivedFrom":subQ0}),1.0]])]});}
            var Q1;
            {var subQ4=sQuery(id+"F12.wireOp",EDGE,"E54");Q1=makeQuery(id+"F12.imprint","IMPRINT",FACE,{"disambiguationData":[TD([[makeQuery(id+"F12.imprint","IMPRINT",EDGE,{"derivedFrom":subQ4}),-1.0]])]});}
            var Q2;
            Q2=makeQuery(id+"F12.imprint","IMPRINT",FACE,{"disambiguationData":[TD([[makeQuery(id+"F12.imprint","IMPRINT",EDGE,{"derivedFrom":sQuery(id+"F12.wireOp",EDGE,"E56.bottom")}),1.0]])]});
            extrude(context, id + "F13", {"entities" : qUnion([Q0, Q1, Q2]), "operationType" : NewBodyOperationType.REMOVE, "oppositeDirection" : true, "depth" : 3.05 * mm, "offsetDistance" : 30.48 * mm});
        }
        {
            var Q0;
            {var subQ5=sQuery(id+"F6.wireOp",EDGE,"E8");Q0=makeQuery(id+"F13.boolean.opBoolean","SPLIT",FACE,{"disambiguationData":[TD([makeQuery(id+"F3.boolean.opBoolean","COPY",FACE,{"derivedFrom":makeQuery(id+"F3.opExtrude","SWEPT_FACE",FACE,{"disambiguationData":[OSD([sQuery(id+"F2.wireOp",EDGE,"E5.top")])]})})])],"derivedFrom":makeQuery(id+"F7.boolean.opBoolean","COPY",FACE,{"derivedFrom":makeQuery(id+"F7.opExtrude","SWEPT_FACE",FACE,{"disambiguationData":[OSD([subQ5])]})})});}
            var sketch = newSketch(context, id + "F14", { "sketchPlane" : qUnion([Q0])});
            skCircle(sketch, "E57", {"center": v(203.2, -1344.73) * mm, "radius": 76.2 * mm});
            skCircle(sketch, "E58", {"center": v(-203.2, -1344.73) * mm, "radius": 76.2 * mm});
            skCircle(sketch, "E59", {"center": v(203.2, -1743.91) * mm, "radius": 76.2 * mm});
            skCircle(sketch, "E60", {"center": v(-203.2, -1743.91) * mm, "radius": 76.2 * mm});
            skSolve(sketch);
        }
        {
            var Q0;
            Q0=makeQuery(id+"F14.imprint","IMPRINT",FACE,{"disambiguationData":[TD([[makeQuery(id+"F14.imprint","IMPRINT",EDGE,{"derivedFrom":sQuery(id+"F14.wireOp",EDGE,"E57")}),1.0]])]});
            var Q1;
            Q1=makeQuery(id+"F14.imprint","IMPRINT",FACE,{"disambiguationData":[TD([[makeQuery(id+"F14.imprint","IMPRINT",EDGE,{"derivedFrom":sQuery(id+"F14.wireOp",EDGE,"E59")}),1.0]])]});
            var Q2;
            Q2=makeQuery(id+"F14.imprint","IMPRINT",FACE,{"disambiguationData":[TD([[makeQuery(id+"F14.imprint","IMPRINT",EDGE,{"derivedFrom":sQuery(id+"F14.wireOp",EDGE,"E60")}),1.0]])]});
            var Q3;
            Q3=makeQuery(id+"F14.imprint","IMPRINT",FACE,{"disambiguationData":[TD([[makeQuery(id+"F14.imprint","IMPRINT",EDGE,{"derivedFrom":sQuery(id+"F14.wireOp",EDGE,"E58")}),1.0]])]});
            extrude(context, id + "F15", {"entities" : qUnion([Q0, Q1, Q2, Q3]), "operationType" : NewBodyOperationType.REMOVE, "oppositeDirection" : true, "depth" : 3.05 * mm, "offsetDistance" : 30.48 * mm});
        }
        {
            var Q0;
            {var subQ2=sQuery(id+"F8.wireOp",EDGE,"E16.left");var subQ3=sQuery(id+"F8.wireOp",EDGE,"E16.bottom");var subQ4=sQuery(id+"F6.wireOp",EDGE,"E8");Q0=makeQuery(id+"F13.boolean.opBoolean","SPLIT",FACE,{"disambiguationData":[TD([makeQuery(id+"F13.opExtrude","SWEPT_FACE",FACE,{"disambiguationData":[OSD([subQ4,subQ3,subQ2,sQuery(id+"F12.wireOp",EDGE,"E52")])]})])],"derivedFrom":makeQuery(id+"F7.boolean.opBoolean","COPY",FACE,{"derivedFrom":makeQuery(id+"F7.opExtrude","SWEPT_FACE",FACE,{"disambiguationData":[OSD([subQ4])]})})});}
            var sketch = newSketch(context, id + "F16", { "sketchPlane" : qUnion([Q0])});
            skLineSegment(sketch, "E61.bottom", {"start": v(355.6, 320.5) * mm, "end": v(-327.15, 320.5) * mm});
            skLineSegment(sketch, "E61.top", {"start": v(355.6, -501.45) * mm, "end": v(-327.15, -501.45) * mm});
            skLineSegment(sketch, "E61.left", {"start": v(355.6, 320.5) * mm, "end": v(355.6, -501.45) * mm});
            skLineSegment(sketch, "E61.right", {"start": v(-327.15, 320.5) * mm, "end": v(-327.15, -501.45) * mm});
            skSolve(sketch);
        }
        {
            var Q0;
            Q0=makeQuery(id+"F16.imprint","IMPRINT",FACE,{"disambiguationData":[TD([[makeQuery(id+"F16.imprint","IMPRINT",EDGE,{"derivedFrom":sQuery(id+"F16.wireOp",EDGE,"E61.bottom")}),1.0]])]});
            extrude(context, id + "F17", {"entities" : qUnion([Q0]), "operationType" : NewBodyOperationType.REMOVE, "oppositeDirection" : true, "depth" : 228.6 * mm, "offsetDistance" : 30.48 * mm});
        }
        {
            var Q0;
            {var subQ0=sQuery(id+"F0.wireOp",EDGE,"E0.right");var subQ3=sQuery(id+"F0.wireOp",EDGE,"E0.bottom");Q0=makeQuery(id+"F9.boolean.opBoolean","SPLIT",FACE,{"disambiguationData":[TD([makeQuery(id+"F1.opExtrude","SWEPT_FACE",FACE,{"disambiguationData":[OSD([subQ3])]})])],"derivedFrom":makeQuery(id+"F1.opExtrude","SWEPT_FACE",FACE,{"disambiguationData":[OSD([subQ0])]})});}
            var sketch = newSketch(context, id + "F18", { "sketchPlane" : qUnion([Q0])});
            skLineSegment(sketch, "E62.bottom", {"start": v(2003, 1917.7) * mm, "end": v(2612.6, 1917.7) * mm});
            skLineSegment(sketch, "E62.top", {"start": v(2003, 622.3) * mm, "end": v(2612.6, 622.3) * mm});
            skLineSegment(sketch, "E62.left", {"start": v(2003, 1917.7) * mm, "end": v(2003, 622.3) * mm});
            skLineSegment(sketch, "E62.right", {"start": v(2612.6, 1917.7) * mm, "end": v(2612.6, 622.3) * mm});
            skLineSegment(sketch, "E63.top", {"start": v(2003, 1308.1) * mm, "end": v(2612.6, 1308.1) * mm});
            skLineSegment(sketch, "E63.left", {"start": v(2003, 1917.7) * mm, "end": v(2003, 1308.1) * mm});
            skLineSegment(sketch, "E63.right", {"start": v(2612.6, 1917.7) * mm, "end": v(2612.6, 1308.1) * mm});
            skLineSegment(sketch, "E64.bottom", {"start": v(2612.6, 622.3) * mm, "end": v(2003, 622.3) * mm});
            skLineSegment(sketch, "E64.top", {"start": v(2612.6, 1231.9) * mm, "end": v(2003, 1231.9) * mm});
            skLineSegment(sketch, "E64.left", {"start": v(2612.6, 622.3) * mm, "end": v(2612.6, 1231.9) * mm});
            skLineSegment(sketch, "E64.right", {"start": v(2003, 622.3) * mm, "end": v(2003, 1231.9) * mm});
            skLineSegment(sketch, "E65.bottom", {"start": v(2003, 2057.4) * mm, "end": v(2612.6, 2057.4) * mm});
            skLineSegment(sketch, "E65.top", {"start": v(2003, 2667) * mm, "end": v(2612.6, 2667) * mm});
            skLineSegment(sketch, "E65.left", {"start": v(2003, 2057.4) * mm, "end": v(2003, 2667) * mm});
            skLineSegment(sketch, "E65.right", {"start": v(2612.6, 2057.4) * mm, "end": v(2612.6, 2667) * mm});
            skLineSegment(sketch, "E66.bottom", {"start": v(1926.9, 101.6) * mm, "end": v(2688.8, 101.6) * mm});
            skLineSegment(sketch, "E66.top", {"start": v(1926.9, 98.55) * mm, "end": v(2688.8, 98.55) * mm});
            skLineSegment(sketch, "E66.left", {"start": v(1926.9, 101.6) * mm, "end": v(1926.9, 98.55) * mm});
            skLineSegment(sketch, "E66.right", {"start": v(2688.8, 101.6) * mm, "end": v(2688.8, 98.55) * mm});
            skLineSegment(sketch, "E67.bottom", {"start": v(2003, 520.7) * mm, "end": v(2612.6, 520.7) * mm});
            skLineSegment(sketch, "E67.top", {"start": v(2003, 177.8) * mm, "end": v(2612.6, 177.8) * mm});
            skLineSegment(sketch, "E67.left", {"start": v(2003, 520.7) * mm, "end": v(2003, 177.8) * mm});
            skLineSegment(sketch, "E67.right", {"start": v(2612.6, 520.7) * mm, "end": v(2612.6, 177.8) * mm});
            skLineSegment(sketch, "E68.bottom", {"start": v(2155.4, 1765.3) * mm, "end": v(2460.2, 1765.3) * mm});
            skLineSegment(sketch, "E68.top", {"start": v(2155.4, 1460.5) * mm, "end": v(2460.2, 1460.5) * mm});
            skLineSegment(sketch, "E68.left", {"start": v(2155.4, 1765.3) * mm, "end": v(2155.4, 1460.5) * mm});
            skLineSegment(sketch, "E68.right", {"start": v(2460.2, 1765.3) * mm, "end": v(2460.2, 1460.5) * mm});
            skLineSegment(sketch, "E69.bottom", {"start": v(2155.4, 1079.5) * mm, "end": v(2460.2, 1079.5) * mm});
            skLineSegment(sketch, "E69.top", {"start": v(2155.4, 774.7) * mm, "end": v(2460.2, 774.7) * mm});
            skLineSegment(sketch, "E69.left", {"start": v(2155.4, 1079.5) * mm, "end": v(2155.4, 774.7) * mm});
            skLineSegment(sketch, "E69.right", {"start": v(2460.2, 1079.5) * mm, "end": v(2460.2, 774.7) * mm});
            skSolve(sketch);
        }
        {
            var Q0;
            Q0=makeQuery(id+"F18.imprint","IMPRINT",FACE,{"disambiguationData":[TD([[makeQuery(id+"F18.imprint","IMPRINT",EDGE,{"derivedFrom":sQuery(id+"F18.wireOp",EDGE,"E65.bottom")}),1.0]])]});
            var Q1;
            {var subQ2=sQuery(id+"F18.wireOp",EDGE,"E62.bottom");Q1=makeQuery(id+"F18.imprint","IMPRINT",FACE,{"disambiguationData":[TD([[makeQuery(id+"F18.imprint","IMPRINT",EDGE,{"derivedFrom":subQ2}),-1.0]])]});}
            var Q2;
            {var subQ2=sQuery(id+"F18.wireOp",EDGE,"E62.top");Q2=makeQuery(id+"F18.imprint","IMPRINT",FACE,{"disambiguationData":[TD([[makeQuery(id+"F18.imprint","IMPRINT",EDGE,{"derivedFrom":subQ2}),1.0]])]});}
            var Q3;
            Q3=makeQuery(id+"F18.imprint","IMPRINT",FACE,{"disambiguationData":[TD([[makeQuery(id+"F18.imprint","IMPRINT",EDGE,{"derivedFrom":sQuery(id+"F18.wireOp",EDGE,"E67.bottom")}),-1.0]])]});
            var Q4;
            {var subQ0=sQuery(id+"F18.wireOp",EDGE,"E66.top");Q4=makeQuery(id+"F18.imprint","IMPRINT",FACE,{"disambiguationData":[TD([[makeQuery(id+"F18.imprint","IMPRINT",EDGE,{"derivedFrom":subQ0}),-1.0]])]});}
            extrude(context, id + "F19", {"entities" : qUnion([Q0, Q1, Q2, Q3, Q4]), "operationType" : NewBodyOperationType.REMOVE, "oppositeDirection" : true, "depth" : 3.05 * mm, "offsetDistance" : 30.48 * mm});
        }
    });
